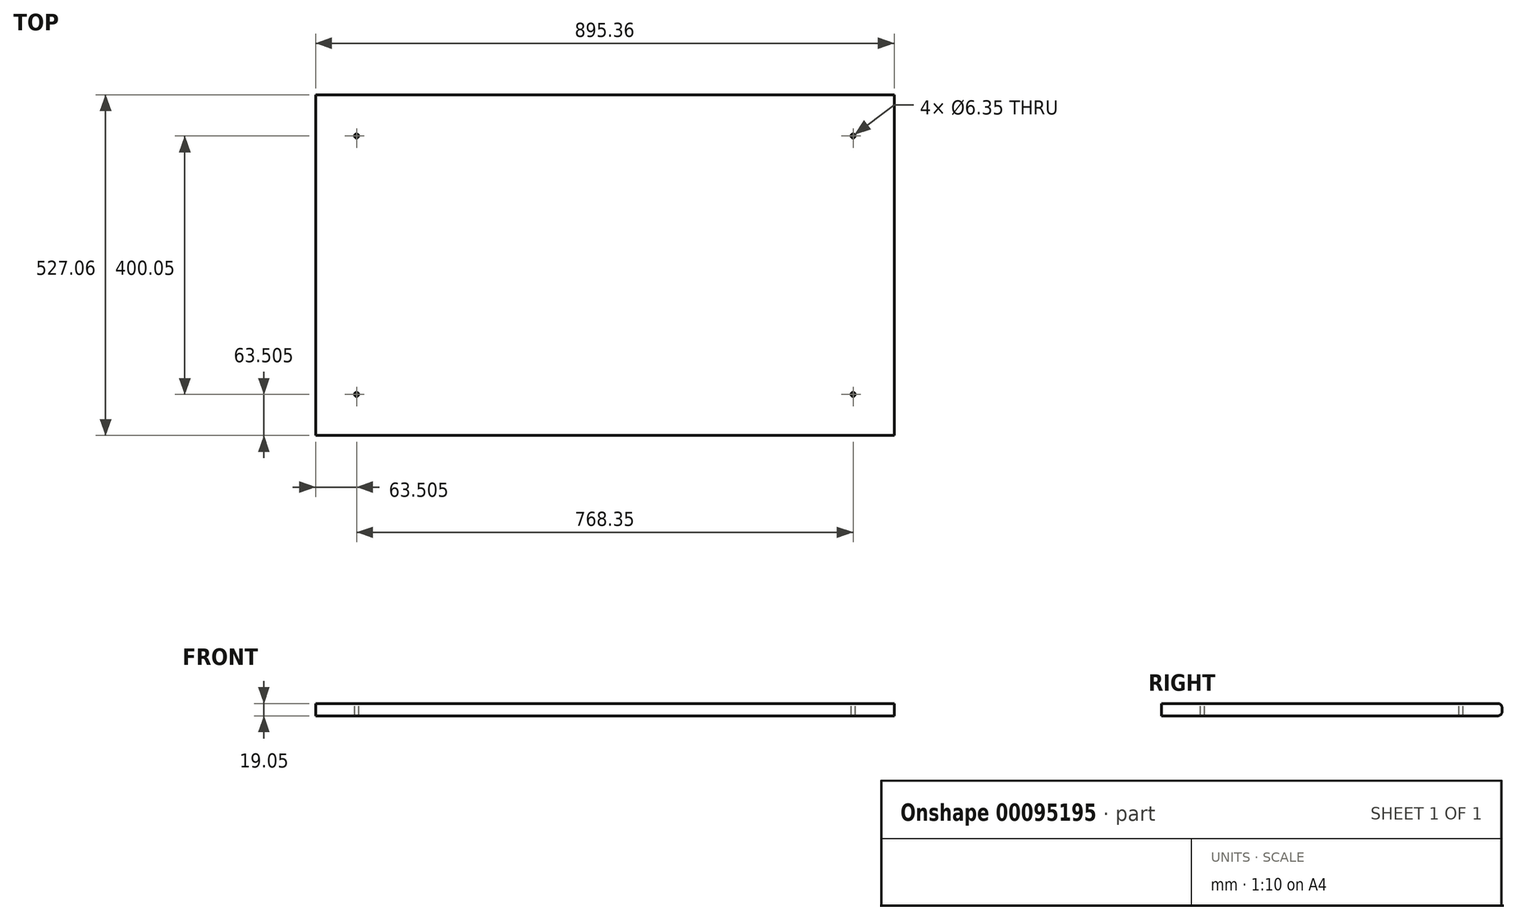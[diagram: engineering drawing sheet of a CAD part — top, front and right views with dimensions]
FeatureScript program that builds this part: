
annotation { "Feature Type Name" : "Feature", "Feature Type Description" : "" }
export const myFeature = defineFeature(function(context is Context, id is Id, definition is map)
    precondition{}
    {
        {
            var Q0;
            Q0=qCreatedBy(makeId("Top.planeOp"),FACE);
            var sketch = newSketch(context, id + "F0", { "sketchPlane" : qUnion([Q0])});
            skLineSegment(sketch, "E0.bottom", {"start": v(447.68, -263.52) * mm, "end": v(-447.68, -263.53) * mm});
            skLineSegment(sketch, "E0.top", {"start": v(447.68, 263.53) * mm, "end": v(-447.68, 263.53) * mm});
            skLineSegment(sketch, "E0.left", {"start": v(447.68, -263.52) * mm, "end": v(447.68, 263.53) * mm});
            skLineSegment(sketch, "E0.right", {"start": v(-447.68, -263.53) * mm, "end": v(-447.68, 263.53) * mm});
            skPoint(sketch, "E0.middle", {"position": v(0, 0) * mm});
            skSolve(sketch);
        }
        {
            var Q0;
            Q0=makeQuery(id+"F0.imprint","IMPRINT",FACE,{"disambiguationData":[TD([[makeQuery(id+"F0.imprint","IMPRINT",EDGE,{"derivedFrom":sQuery(id+"F0.wireOp",EDGE,"E0.bottom")}),-1.0]])]});
            extrude(context, id + "F1", {"entities" : qUnion([Q0]), "depth" : 19.05 * mm});
        }
        {
            var Q0;
            Q0=makeQuery(id+"F1.opExtrude","CAP_EDGE",EDGE,{"disambiguationData":[OSD([sQuery(id+"F0.wireOp",EDGE,"E0.top")])],"isStart":false});
            var Q1;
            Q1=makeQuery(id+"F1.opExtrude","CAP_EDGE",EDGE,{"disambiguationData":[OSD([sQuery(id+"F0.wireOp",EDGE,"E0.top")])],"isStart":true});
            fillet(context, id + "F2", {"entities" : qUnion([Q0, Q1]), "radius" : 6.35 * mm, "tangentPropagation" : true, "allowEdgeOverflow" : false});
        }
        {
            var Q0;
            Q0=makeQuery(id+"F1.opExtrude","CAP_FACE",FACE,{"disambiguationData":[OSD([sQuery(id+"F0.wireOp",EDGE,"E0.bottom"),sQuery(id+"F0.wireOp",EDGE,"E0.top"),sQuery(id+"F0.wireOp",EDGE,"E0.left"),sQuery(id+"F0.wireOp",EDGE,"E0.right")])],"isStart":false});
            var sketch = newSketch(context, id + "F3", { "sketchPlane" : qUnion([Q0])});
            skLineSegment(sketch, "E1.bottom", {"start": v(-447.68, -263.53) * mm, "end": v(-384.18, -263.53) * mm, "construction": true});
            skLineSegment(sketch, "E1.top", {"start": v(-447.68, -200.03) * mm, "end": v(-384.18, -200.03) * mm, "construction": true});
            skLineSegment(sketch, "E1.left", {"start": v(-447.68, -263.53) * mm, "end": v(-447.68, -200.03) * mm, "construction": true});
            skLineSegment(sketch, "E1.right", {"start": v(-384.18, -263.53) * mm, "end": v(-384.18, -200.03) * mm, "construction": true});
            skLineSegment(sketch, "E2.bottom", {"start": v(447.68, -263.52) * mm, "end": v(384.18, -263.52) * mm, "construction": true});
            skLineSegment(sketch, "E2.top", {"start": v(447.68, -200.02) * mm, "end": v(384.18, -200.02) * mm, "construction": true});
            skLineSegment(sketch, "E2.left", {"start": v(447.68, -263.52) * mm, "end": v(447.68, -200.02) * mm, "construction": true});
            skLineSegment(sketch, "E2.right", {"start": v(384.18, -263.52) * mm, "end": v(384.18, -200.02) * mm, "construction": true});
            skLineSegment(sketch, "E3.bottom", {"start": v(447.68, 257.18) * mm, "end": v(384.18, 257.18) * mm, "construction": true});
            skLineSegment(sketch, "E3.top", {"start": v(447.68, 200.03) * mm, "end": v(384.18, 200.03) * mm, "construction": true});
            skLineSegment(sketch, "E3.left", {"start": v(447.68, 257.18) * mm, "end": v(447.68, 200.03) * mm, "construction": true});
            skLineSegment(sketch, "E3.right", {"start": v(384.18, 257.18) * mm, "end": v(384.18, 200.03) * mm, "construction": true});
            skLineSegment(sketch, "E4.bottom", {"start": v(-447.68, 257.18) * mm, "end": v(-384.18, 257.18) * mm, "construction": true});
            skLineSegment(sketch, "E4.top", {"start": v(-447.68, 200.02) * mm, "end": v(-384.18, 200.02) * mm, "construction": true});
            skLineSegment(sketch, "E4.left", {"start": v(-447.68, 257.18) * mm, "end": v(-447.68, 200.02) * mm, "construction": true});
            skLineSegment(sketch, "E4.right", {"start": v(-384.18, 257.18) * mm, "end": v(-384.18, 200.02) * mm, "construction": true});
            skSolve(sketch);
        }
        {
            var Q0;
            Q0=sQuery(id+"F3.wireOp",VERTEX,"E1.right.end");
            var Q1;
            Q1=sQuery(id+"F3.wireOp",VERTEX,"E4.top.end");
            var Q2;
            Q2=sQuery(id+"F3.wireOp",VERTEX,"E3.right.end");
            var Q3;
            Q3=sQuery(id+"F3.wireOp",VERTEX,"E2.right.end");
            var Q4;
            Q4=makeQuery(id+"F1.opExtrude","SWEPT_BODY",BODY,{"disambiguationData":[OSD([sQuery(id+"F0.wireOp",EDGE,"E0.bottom"),sQuery(id+"F0.wireOp",EDGE,"E0.top"),sQuery(id+"F0.wireOp",EDGE,"E0.left"),sQuery(id+"F0.wireOp",EDGE,"E0.right")])]});
            hole(context, id + "F4", {"style" : HoleStyle.SIMPLE, "endStyle" : HoleEndStyle.THROUGH, "holeDiameter" : 6.35 * mm, "startFromSketch" : true, "locations" : qUnion([Q0, Q1, Q2, Q3]), "scope" : qUnion([Q4]), "isTappedThrough" : true});
        }
    });
